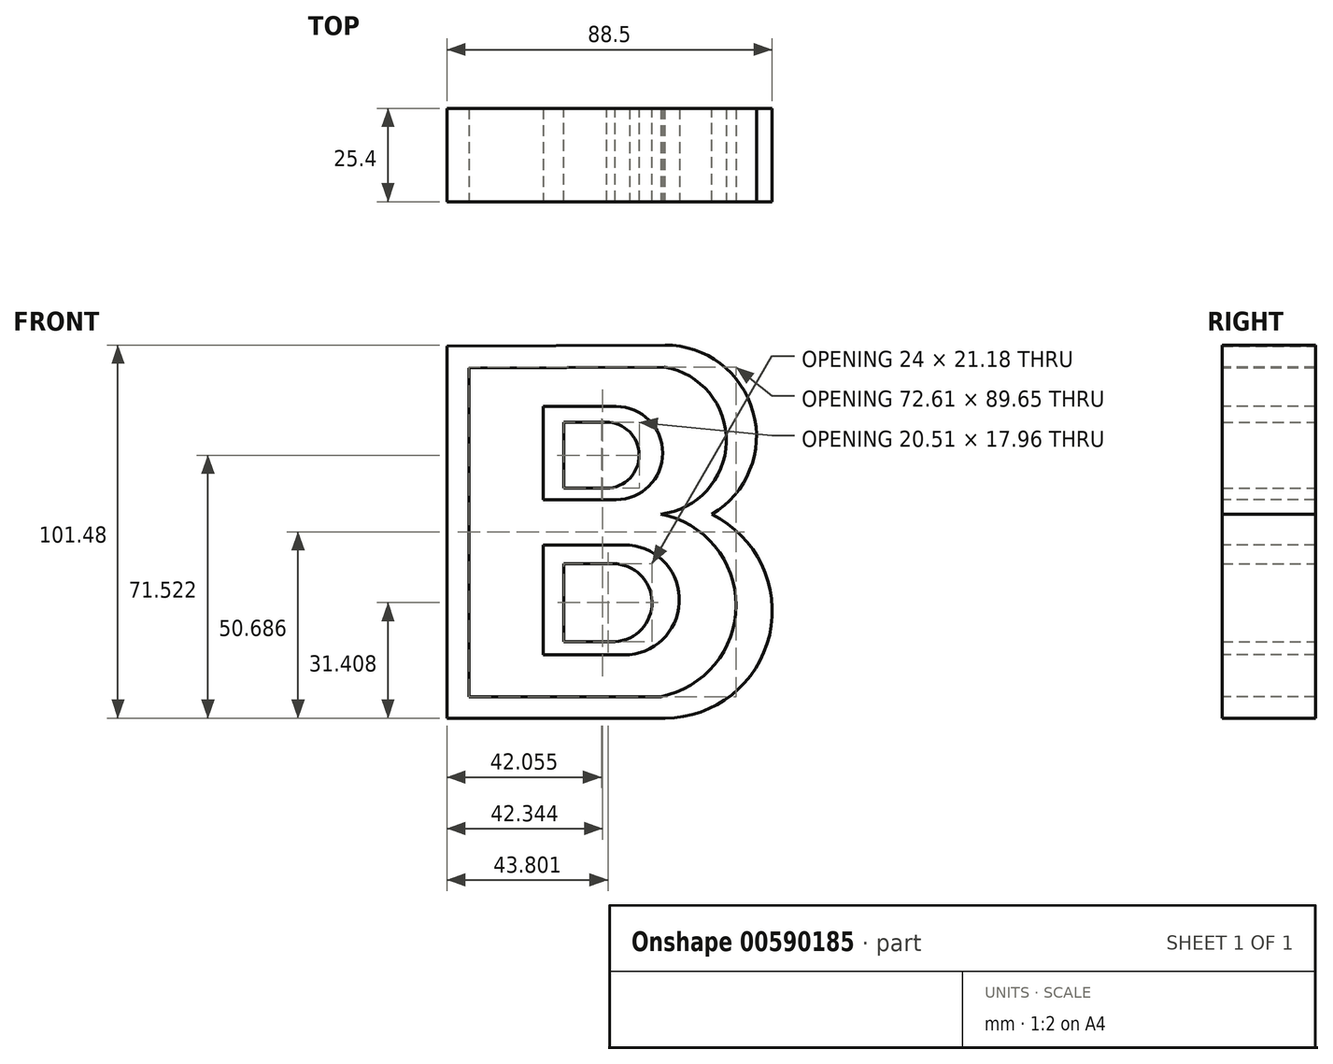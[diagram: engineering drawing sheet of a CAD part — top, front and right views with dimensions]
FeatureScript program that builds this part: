
annotation { "Feature Type Name" : "Feature", "Feature Type Description" : "" }
export const myFeature = defineFeature(function(context is Context, id is Id, definition is map)
    precondition{}
    {
        {
            var Q0;
            Q0=qCreatedBy(makeId("Front.planeOp"),FACE);
            var sketch = newSketch(context, id + "F0", { "sketchPlane" : qUnion([Q0])});
            skLineSegment(sketch, "E0", {"start": v(-89.9, 48.4) * mm, "end": v(-89.9, -52.82) * mm});
            skLineSegment(sketch, "E1", {"start": v(-89.9, -52.82) * mm, "end": v(-30.57, -52.82) * mm});
            skLineSegment(sketch, "E2", {"start": v(-30.57, 48.66) * mm, "end": v(-89.9, 48.4) * mm});
            skArc(sketch, "E3", {"start": v(-17.82, 2.6) * mm, "mid": v(-6.6, 30.5) * mm, "end": v(-30.57, 48.66) * mm});
            skArc(sketch, "E4", {"start": v(-30.57, -52.82) * mm, "mid": v(-2.14, -30.18) * mm, "end": v(-17.82, 2.6) * mm});
            skSolve(sketch);
        }
        {
            var Q0;
            Q0=qSketchRegion(id+"F0",true);
            extrude(context, id + "F1", {"entities" : qUnion([Q0]), "depth" : 25.4 * mm, "offsetDistance" : 25.4 * mm});
        }
        {
            var Q0;
            Q0=makeQuery(id+"F0.imprint","IMPRINT",FACE,{"disambiguationData":[TD([[makeQuery(id+"F0.imprint","IMPRINT",EDGE,{"derivedFrom":sQuery(id+"F0.wireOp",EDGE,"E0")}),1.0]])]});
            var sketch = newSketch(context, id + "F2", { "sketchPlane" : qUnion([Q0])});
            skLineSegment(sketch, "E5", {"start": v(-58.1, 27.68) * mm, "end": v(-58.1, 9.72) * mm});
            skLineSegment(sketch, "E6", {"start": v(-58.1, 27.68) * mm, "end": v(-46.57, 27.68) * mm});
            skLineSegment(sketch, "E7", {"start": v(-58.1, 9.72) * mm, "end": v(-46.38, 9.72) * mm});
            skLineSegment(sketch, "E8", {"start": v(-58.1, -10.82) * mm, "end": v(-58.1, -32) * mm});
            skLineSegment(sketch, "E9", {"start": v(-58.1, -32) * mm, "end": v(-44.13, -32) * mm});
            skLineSegment(sketch, "E10", {"start": v(-58.1, -10.82) * mm, "end": v(-44.7, -10.82) * mm});
            skArc(sketch, "E11", {"start": v(-46.38, 9.72) * mm, "mid": v(-37.6, 18.8) * mm, "end": v(-46.57, 27.68) * mm});
            skArc(sketch, "E12", {"start": v(-44.13, -32) * mm, "mid": v(-34.1, -21.14) * mm, "end": v(-44.7, -10.82) * mm});
            skSolve(sketch);
        }
        {
            var Q0;
            Q0=qSketchRegion(id+"F2",true);
            extrude(context, id + "F3", {"entities" : qUnion([Q0]), "operationType" : NewBodyOperationType.REMOVE, "oppositeDirection" : true, "depth" : 25.4 * mm, "offsetDistance" : 25.4 * mm});
        }
        {
            var Q0;
            Q0=qSketchRegion(id+"F2",true);
            extrude(context, id + "F4", {"entities" : qUnion([Q0]), "operationType" : NewBodyOperationType.REMOVE, "depth" : 53.85 * mm, "offsetDistance" : 25.4 * mm});
        }
        {
            var Q0;
            Q0=makeQuery(id+"F1.opExtrude","CAP_FACE",FACE,{"disambiguationData":[OSD([sQuery(id+"F0.wireOp",EDGE,"E0"),sQuery(id+"F0.wireOp",EDGE,"E1"),sQuery(id+"F0.wireOp",EDGE,"E2"),sQuery(id+"F0.wireOp",EDGE,"E3"),sQuery(id+"F0.wireOp",EDGE,"E4")])],"isStart":false});
            var sketch = newSketch(context, id + "F5", { "sketchPlane" : qUnion([Q0])});
            skLineSegment(sketch, "E13", {"start": v(-83.86, 42.46) * mm, "end": v(-83.86, -46.96) * mm});
            skLineSegment(sketch, "E14", {"start": v(-83.86, -46.96) * mm, "end": v(-31.74, -46.96) * mm});
            skLineSegment(sketch, "E15", {"start": v(-83.86, 42.46) * mm, "end": v(-30.7, 42.7) * mm});
            skLineSegment(sketch, "E16", {"start": v(-63.67, 31.95) * mm, "end": v(-63.67, 6.6) * mm});
            skLineSegment(sketch, "E17", {"start": v(-63.67, 6.6) * mm, "end": v(-43.9, 6.6) * mm});
            skLineSegment(sketch, "E18", {"start": v(-63.67, -35.63) * mm, "end": v(-63.67, -5.75) * mm});
            skLineSegment(sketch, "E19", {"start": v(-63.67, -5.75) * mm, "end": v(-40.18, -5.75) * mm});
            skLineSegment(sketch, "E20", {"start": v(-63.67, -35.63) * mm, "end": v(-41.63, -35.63) * mm});
            skLineSegment(sketch, "E21", {"start": v(-63.67, 31.95) * mm, "end": v(-43.9, 31.95) * mm});
            skArc(sketch, "E22", {"start": v(-43.9, 6.6) * mm, "mid": v(-31.22, 19.28) * mm, "end": v(-43.9, 31.95) * mm});
            skArc(sketch, "E23", {"start": v(-41.63, -35.63) * mm, "mid": v(-26.67, -21.38) * mm, "end": v(-40.18, -5.75) * mm});
            skArc(sketch, "E24", {"start": v(-31.74, -46.96) * mm, "mid": v(-11.25, -22.13) * mm, "end": v(-31.74, 2.7) * mm});
            skArc(sketch, "E25", {"start": v(-31.74, 2.7) * mm, "mid": v(-13.89, 22.25) * mm, "end": v(-30.7, 42.7) * mm});
            skSolve(sketch);
        }
        {
            var Q0;
            Q0=qSketchRegion(id+"F5",true);
            extrude(context, id + "F6", {"entities" : qUnion([Q0]), "operationType" : NewBodyOperationType.REMOVE, "oppositeDirection" : true, "depth" : 25.4 * mm, "offsetDistance" : 25.4 * mm});
        }
    });
